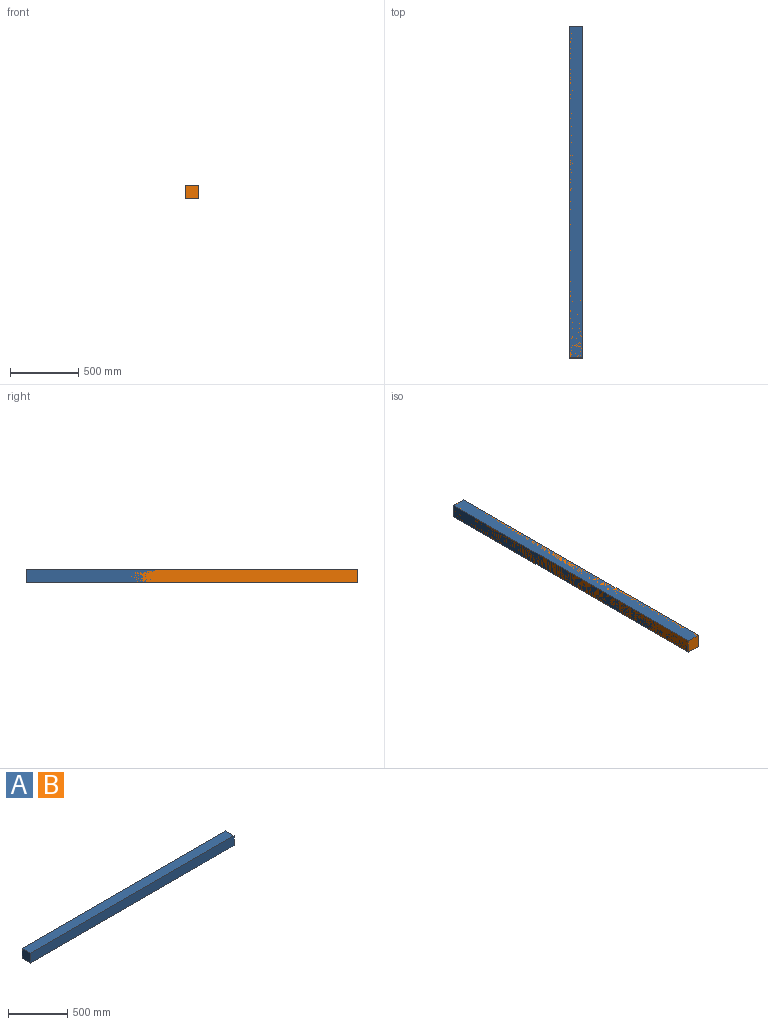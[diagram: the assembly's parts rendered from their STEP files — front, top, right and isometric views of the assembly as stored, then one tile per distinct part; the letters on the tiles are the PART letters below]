
ASSEMBLY  parts=2 mates=1
PART A: 6 faces, bbox 2438.4x101.6x101.6 mm
  f0: plane 2438.4x101.6mm, normal (0,1,0), area 247741.4mm2, adj f1,f3,f4,f5
  f1: plane 2438.4x101.6mm, normal (0,0,1), area 247741.4mm2, adj f0,f2,f4,f5
  f2: plane 2438.4x101.6mm, normal (0,-1,0), area 247741.4mm2, adj f1,f3,f4,f5
  f3: plane 2438.4x101.6mm, normal (0,0,-1), area 247741.4mm2, adj f0,f2,f4,f5
  f4: plane 101.6x101.6mm, normal (1,0,0), area 10322.6mm2, adj f0,f1,f2,f3
  f5: plane 101.6x101.6mm, normal (-1,0,0), area 10322.6mm2, adj f0,f1,f2,f3
PART B: same geometry as A
PLACE A rot(axis=(0,0,1),90deg) t=(512.42,175.83,-180.03)mm
PLACE B rot(axis=(0,0,1),90deg) t=(512.42,175.83,-180.03)mm
MATE planar B.f3 <-> A.f3  axis (0,0,-1) through (512.42,175.83,-230.83)mm
